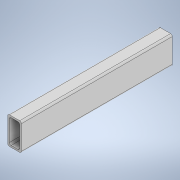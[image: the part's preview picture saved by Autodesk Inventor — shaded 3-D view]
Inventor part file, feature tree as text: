
AUTODESK INVENTOR PART (.ipt)
format: ipt  version: 2020 (Build 240168000, 168)  size: 124,416 bytes
history: native  units: in
note: dims shown in document units (in); Inventor stores cm internally (conversion verified against a paired STEP export)
features: extrude x1, sketch x1
ambient origin geometry x8: Origin, YZ Plane, XZ Plane, XY Plane, X Axis, Y Axis, Z Axis, Center Point
bodies: Solid1 (feature_tree)
feature tree (2):
  extrude  "Extrusion1"  Depth=1.0in
  sketch  "Sketch1"  dims[d0=2.0in d1=1.0in d2=0.125in d3=0.125in d4=0.125in d5=0.125in d6=0.125in d7=0.125in d8=0.125in d9=0.125in d10=0.125in d11=11.0in d12=0.0in]
